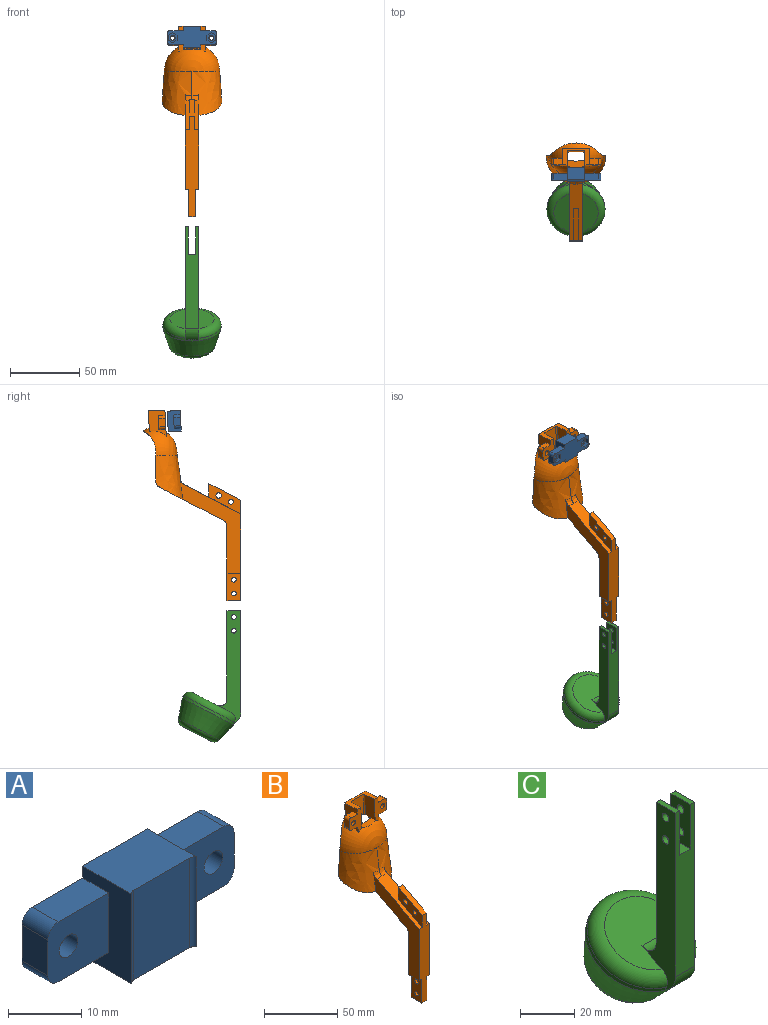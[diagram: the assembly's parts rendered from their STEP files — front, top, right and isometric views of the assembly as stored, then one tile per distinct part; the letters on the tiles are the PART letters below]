
ASSEMBLY  parts=3 mates=2
PART A: 36 faces, bbox 36x9.4x15 mm
  f0: cylinder r=1.8mm len=3.6mm, axis (0,1,0), area 28.3mm2, adj f9,f19
  f1: plane 12.5x9.44mm, normal (0,0,-1), area 112.7mm2, adj f8,f10,f11,f12,f26,f28
  f2: plane 12.5x9.44mm, normal (0,0,1), area 112.7mm2, adj f8,f10,f11,f12,f26,f28
  f3: plane 9.75x5mm, normal (0,0,1), area 48.8mm2, adj f4,f8,f9,f10
  f4: cylinder r=2mm len=5mm, axis (0,1,0), area 15.7mm2, adj f3,f5,f9,f10
  f5: plane 6x5mm, normal (-1,0,0), area 30mm2, adj f4,f6,f9,f10
  f6: cylinder r=2mm len=5mm, axis (0,1,0), area 15.7mm2, adj f5,f7,f9,f10
  f7: plane 9.75x5mm, normal (0,0,-1), area 48.8mm2, adj f6,f8,f9,f10
  f8: plane 15x9.44mm, normal (-1,0,0), area 91.5mm2, adj f1,f2,f3,f7,f9,f10,f11
  f9: plane 11.75x10mm, normal (0,-1,0), area 105.6mm2, adj f0,f3,f4,f5,f6,f7,f8
  f10: plane 36x15mm, normal (0,1,0), area 348.1mm2, adj f1,f2,f3,f4,f5,f6,f7,f8
  f11: cylinder r=1mm len=15mm, axis (0,0,1), area 14.6mm2, adj f1,f2,f8,f12
  f12: plane 15x10.85mm, normal (0,-1,0), area 162.7mm2, adj f1,f2,f11,f28
  f13: plane 3.7x2.5mm, normal (1,0,0), area 9.2mm2, adj f10,f14,f18,f19
  f14: plane 3.2x2.5mm, normal (0.5,0,-0.87), area 9.2mm2, adj f10,f13,f15,f19
  f15: plane 3.2x2.5mm, normal (-0.5,0,-0.87), area 9.2mm2, adj f10,f14,f16,f19
  f16: plane 3.7x2.5mm, normal (-1,0,0), area 9.2mm2, adj f10,f15,f17,f19
  f17: plane 3.2x2.5mm, normal (-0.5,0,0.87), area 9.2mm2, adj f10,f16,f18,f19
  f18: plane 3.2x2.5mm, normal (0.5,0,0.87), area 9.2mm2, adj f10,f13,f17,f19
  f19: plane 7.39x6.4mm, normal (0,1,0), area 25.3mm2, adj f0,f13,f14,f15,f16,f17,f18
  f20: cylinder r=1.8mm len=3.6mm, axis (0,1,0), area 28.3mm2, adj f27,f35
  f21: plane 9.75x5mm, normal (0,0,1), area 48.8mm2, adj f10,f22,f26,f27
  f22: cylinder r=2mm len=5mm, axis (0,1,0), area 15.7mm2, adj f10,f21,f23,f27
  f23: plane 6x5mm, normal (1,0,0), area 30mm2, adj f10,f22,f24,f27
  f24: cylinder r=2mm len=5mm, axis (0,1,0), area 15.7mm2, adj f10,f23,f25,f27
  f25: plane 9.75x5mm, normal (0,0,-1), area 48.8mm2, adj f10,f24,f26,f27
  f26: plane 15x9.44mm, normal (1,0,0), area 91.5mm2, adj f1,f2,f10,f21,f25,f27,f28
  f27: plane 11.75x10mm, normal (0,-1,0), area 105.6mm2, adj f20,f21,f22,f23,f24,f25,f26
  f28: cylinder r=1mm len=15mm, axis (0,0,1), area 14.6mm2, adj f1,f2,f12,f26
  f29: plane 3.7x2.5mm, normal (-1,0,0), area 9.2mm2, adj f10,f30,f34,f35
  f30: plane 3.2x2.5mm, normal (-0.5,0,-0.87), area 9.2mm2, adj f10,f29,f31,f35
  f31: plane 3.2x2.5mm, normal (0.5,0,-0.87), area 9.2mm2, adj f10,f30,f32,f35
  f32: plane 3.7x2.5mm, normal (1,0,0), area 9.2mm2, adj f10,f31,f33,f35
  f33: plane 3.2x2.5mm, normal (0.5,0,0.87), area 9.2mm2, adj f10,f32,f34,f35
  f34: plane 3.2x2.5mm, normal (-0.5,0,0.87), area 9.2mm2, adj f10,f29,f33,f35
  f35: plane 7.39x6.4mm, normal (0,1,0), area 25.3mm2, adj f20,f29,f30,f31,f32,f33,f34
PART B: 68 faces, bbox 48.8x76.5x144 mm
  f0: plane 68.22x44.04mm, normal (1,0,0), area 826.4mm2, adj f1,f5,f16,f17,f18,f56,f58,f65
  f1: plane 72.87x10mm, normal (0,-1,0), area 568.7mm2, adj f0,f8,f17,f37,f39,f55,f61,f62
  f2: offset ~41x27.01mm, area 770.2mm2, adj f4,f5,f8,f14,f16,f57,f59
  f3: bspline ~35x21.01mm, area 669.5mm2, adj f4,f6,f13,f16,f59
  f4: plane 22.26x4.88mm, normal (0,1,0), area 66.9mm2, adj f2,f3,f13,f14,f15,f59
  f5: offset ~41x27.01mm, area 770.2mm2, adj f0,f2,f7,f14,f16,f56,f60
  f6: bspline ~35x21.01mm, area 669.5mm2, adj f3,f7,f13,f16,f60
  f7: plane 22.26x4.88mm, normal (0,1,0), area 66.9mm2, adj f5,f6,f13,f14,f15,f60
  f8: plane 68.23x44.04mm, normal (-1,0,0), area 826.4mm2, adj f1,f2,f16,f17,f18,f57,f58,f61
  f9: cylinder r=1.8mm len=3.75mm, axis (0,-1,0.05), area 33.9mm2, adj f12,f33
  f10: plane 18.95x12.98mm, normal (-1,0,0), area 140.9mm2, adj f11,f12,f14,f20,f27,f28,f29
  f11: plane 20x11.98mm, normal (0,0.05,1), area 110.4mm2, adj f10,f12,f20,f22,f23,f24,f41,f42
  f12: plane 18.97x11.52mm, normal (0,-1,0.05), area 130.6mm2, adj f9,f10,f11,f14,f24,f27,f28,f30
  f13: revolved ~34.29x18.79mm, area 807.1mm2, adj f3,f4,f6,f7,f15,f19,f21,f22
  f14: revolved ~40.29x24.51mm, area 1043.7mm2, adj f2,f4,f5,f7,f10,f12,f15,f20
  f15: cylinder r=15mm len=39.44mm, axis (1,0,0), area 165.5mm2, adj f4,f7,f13,f14
  f16: plane 49.49x46.16mm, normal (0,0.46,-0.89), area 524.3mm2, adj f0,f2,f3,f5,f6,f8,f58,f59
  f17: plane 41.26x21.48mm, normal (0,-0.46,0.89), area 358.1mm2, adj f0,f1,f8,f35,f39,f55,f56,f57
  f18: plane 53.76x10mm, normal (0,1,0), area 437.6mm2, adj f0,f8,f58,f61,f62,f63,f64,f65
  f19: cylinder r=13.08mm len=3.46mm, axis (1,0,0), area 5.6mm2, adj f13,f22
  f20: plane 20.29x15.28mm, normal (0,1,-0.05), area 264mm2, adj f10,f11,f14,f41
  f21: plane 2.36x0.69mm, normal (0,1,-0.05), area 0.7mm2, adj f13,f25,f26
  f22: plane 16.04x11.02mm, normal (0,-1,0.05), area 170mm2, adj f11,f13,f19,f23,f44
  f23: cylinder r=1mm len=16.49mm, axis (0,0.05,1), area 25.5mm2, adj f11,f13,f22,f24
  f24: plane 17.98x10.09mm, normal (1,0,0), area 152.2mm2, adj f11,f12,f13,f23,f25,f26
  f25: cylinder r=1mm len=1.03mm, axis (0,0.05,1), area 1mm2, adj f13,f21,f24,f26
  f26: plane 14.32x7.85mm, normal (0,0.05,1), area 63.4mm2, adj f13,f14,f21,f24,f25,f43,f45,f46
  f27: plane 6x4.99mm, normal (0,-0.05,-1), area 30mm2, adj f10,f12,f29,f32
  f28: plane 6x4.99mm, normal (0,0.05,1), area 30mm2, adj f10,f12,f29,f30
  f29: plane 9.99x8mm, normal (0,1,-0.05), area 43.1mm2, adj f10,f27,f28,f30,f31,f32,f34
  f30: cylinder r=2mm len=5.1mm, axis (0,-1,0.05), area 15.7mm2, adj f12,f28,f29,f31
  f31: plane 6.25x5.31mm, normal (-1,0,0), area 30mm2, adj f12,f29,f30,f32
  f32: cylinder r=2mm len=5.1mm, axis (0,-1,0.05), area 15.7mm2, adj f12,f27,f29,f31
  f33: plane 6.69x6.68mm, normal (0,1,-0.05), area 25mm2, adj f9,f34
  f34: cylinder r=3.35mm len=6.79mm, axis (0,1,-0.05), area 42mm2, adj f29,f33
  f35: plane 10x4mm, normal (0,1,0), area 40mm2, adj f17,f37,f39,f55
  f36: cylinder r=1.7mm len=4mm, axis (1,0,0), area 42.8mm2, adj f39,f55
  f37: plane 23.06x12.01mm, normal (0,-0.46,0.89), area 104mm2, adj f1,f35,f39,f55
  f38: cylinder r=1.98mm len=4mm, axis (1,0,0), area 49.9mm2, adj f39,f55
  f39: plane 23.06x22.01mm, normal (-1,0,0), area 209.1mm2, adj f1,f17,f35,f36,f37,f38
  f40: cylinder r=1.8mm len=3.75mm, axis (0,-1,0.05), area 33.9mm2, adj f42,f53
  f41: plane 18.95x12.98mm, normal (1,0,0), area 140.9mm2, adj f11,f14,f20,f42,f47,f48,f49
  f42: plane 18.97x11.52mm, normal (0,-1,0.05), area 130.6mm2, adj f11,f14,f40,f41,f45,f47,f48,f50
  f43: plane 2.36x0.69mm, normal (0,1,-0.05), area 0.7mm2, adj f13,f26,f46
  f44: cylinder r=1mm len=16.49mm, axis (0,0.05,1), area 25.5mm2, adj f11,f13,f22,f45
  f45: plane 17.98x10.09mm, normal (-1,0,0), area 152.2mm2, adj f11,f13,f26,f42,f44,f46
  f46: cylinder r=1mm len=1.03mm, axis (0,0.05,1), area 1mm2, adj f13,f26,f43,f45
  f47: plane 6x4.99mm, normal (0,-0.05,-1), area 30mm2, adj f41,f42,f49,f52
  f48: plane 6x4.99mm, normal (0,0.05,1), area 30mm2, adj f41,f42,f49,f50
  f49: plane 9.99x8mm, normal (0,1,-0.05), area 43.1mm2, adj f41,f47,f48,f50,f51,f52,f54
  f50: cylinder r=2mm len=5.1mm, axis (0,-1,0.05), area 15.7mm2, adj f42,f48,f49,f51
  f51: plane 6.25x5.31mm, normal (1,0,0), area 30mm2, adj f42,f49,f50,f52
  f52: cylinder r=2mm len=5.1mm, axis (0,-1,0.05), area 15.7mm2, adj f42,f47,f49,f51
  f53: plane 6.69x6.68mm, normal (0,1,-0.05), area 25mm2, adj f40,f54
  f54: cylinder r=3.35mm len=6.79mm, axis (0,1,-0.05), area 42mm2, adj f49,f53
  f55: plane 23.06x22.01mm, normal (1,0,0), area 209.1mm2, adj f1,f17,f35,f36,f37,f38
  f56: bspline ~14.46x4.18mm, area 23.9mm2, adj f0,f5,f17,f57
  f57: bspline ~14.46x4.18mm, area 23.9mm2, adj f2,f8,f17,f56
  f58: cylinder r=5mm len=10mm, axis (-1,0,0), area 54.5mm2, adj f0,f8,f16,f18
  f59: cylinder r=5mm len=4.44mm, axis (1,0,0), area 16.6mm2, adj f2,f3,f4,f16
  f60: cylinder r=5mm len=4.44mm, axis (1,0,0), area 16.6mm2, adj f5,f6,f7,f16
  f61: plane 10x2.5mm, normal (0,0,-1), area 25mm2, adj f1,f8,f18,f62
  f62: plane 20x10mm, normal (-1,0,0), area 181.8mm2, adj f1,f18,f61,f63,f66,f67
  f63: plane 10x5mm, normal (0,0,-1), area 50mm2, adj f1,f18,f62,f64
  f64: plane 20x10mm, normal (1,0,0), area 181.8mm2, adj f1,f18,f63,f65,f66,f67
  f65: plane 10x2.5mm, normal (0,0,-1), area 25mm2, adj f0,f1,f18,f64
  f66: cylinder r=1.7mm len=5mm, axis (-1,0,0), area 53.4mm2, adj f62,f64
  f67: cylinder r=1.7mm len=5mm, axis (-1,0,0), area 53.4mm2, adj f62,f64
PART C: 21 faces, bbox 45.5x46x95.3 mm
  f0: plane 23.6x20.93mm, normal (0,0.46,-0.89), area 437.4mm2, adj f1
  f1: torus R=11.8mm, axis (0,0.46,-0.89), area 583.5mm2, adj f0,f2
  f2: cone r=15.5mm half-angle=17deg, axis (0,-0.46,0.89), area 1785.3mm2, adj f1,f5
  f3: plane 32x27.67mm, normal (0,-0.46,0.89), area 681.5mm2, adj f4,f7,f10,f11
  f4: torus R=16mm, axis (0,0.46,-0.89), area 867.2mm2, adj f3,f5,f10,f11
  f5: cylinder r=21mm len=42mm, axis (0,-0.46,0.89), area 253.3mm2, adj f2,f4,f6,f10,f11
  f6: cylinder r=9mm len=10mm, axis (1,0,0), area 96.8mm2, adj f5,f8,f10,f11
  f7: cylinder r=5mm len=10mm, axis (-1,0,0), area 102.5mm2, adj f3,f9,f10,f11
  f8: plane 73.75x10mm, normal (0,-1,0), area 627.5mm2, adj f6,f10,f11,f12,f13,f14,f15,f16
  f9: plane 63.86x10mm, normal (0,1,0), area 528.6mm2, adj f7,f10,f11,f12,f13,f14,f15,f16
  f10: plane 81.97x17.31mm, normal (1,0,0), area 758.7mm2, adj f3,f4,f5,f6,f7,f8,f9,f16
  f11: plane 81.97x17.31mm, normal (-1,0,0), area 758.7mm2, adj f3,f4,f5,f6,f7,f8,f9,f12
  f12: plane 10x2.25mm, normal (0,0,1), area 22.5mm2, adj f8,f9,f11,f13
  f13: plane 20x10mm, normal (1,0,0), area 181.8mm2, adj f8,f9,f12,f14,f19,f20
  f14: plane 10x5.5mm, normal (0,0,1), area 55mm2, adj f8,f9,f13,f15
  f15: plane 20x10mm, normal (-1,0,0), area 181.8mm2, adj f8,f9,f14,f16,f17,f18
  f16: plane 10x2.25mm, normal (0,0,1), area 22.5mm2, adj f8,f9,f10,f15
  f17: cylinder r=1.7mm len=3.4mm, axis (-1,0,0), area 24mm2, adj f10,f15
  f18: cylinder r=1.7mm len=3.4mm, axis (-1,0,0), area 24mm2, adj f10,f15
  f19: cylinder r=1.7mm len=3.4mm, axis (-1,0,0), area 24mm2, adj f11,f13
  f20: cylinder r=1.7mm len=3.4mm, axis (-1,0,0), area 24mm2, adj f11,f13
PLACE A rot(axis=(1,0,0),177deg) t=(-57.05,49.04,95.84)mm
PLACE B rot(axis=(1,0,0),0deg) t=(-57.05,70.3,29.45)mm
PLACE C t=(-57.05,70.3,2.6)mm
MATE slider B.f63 <-> C.f14  axis (0,0,-1) through (-57.05,10.3,-40.76)mm
MATE slider B.f40 <-> A.f20  axis (0,-1,0.05) through (-43.05,59.66,88.29)mm
